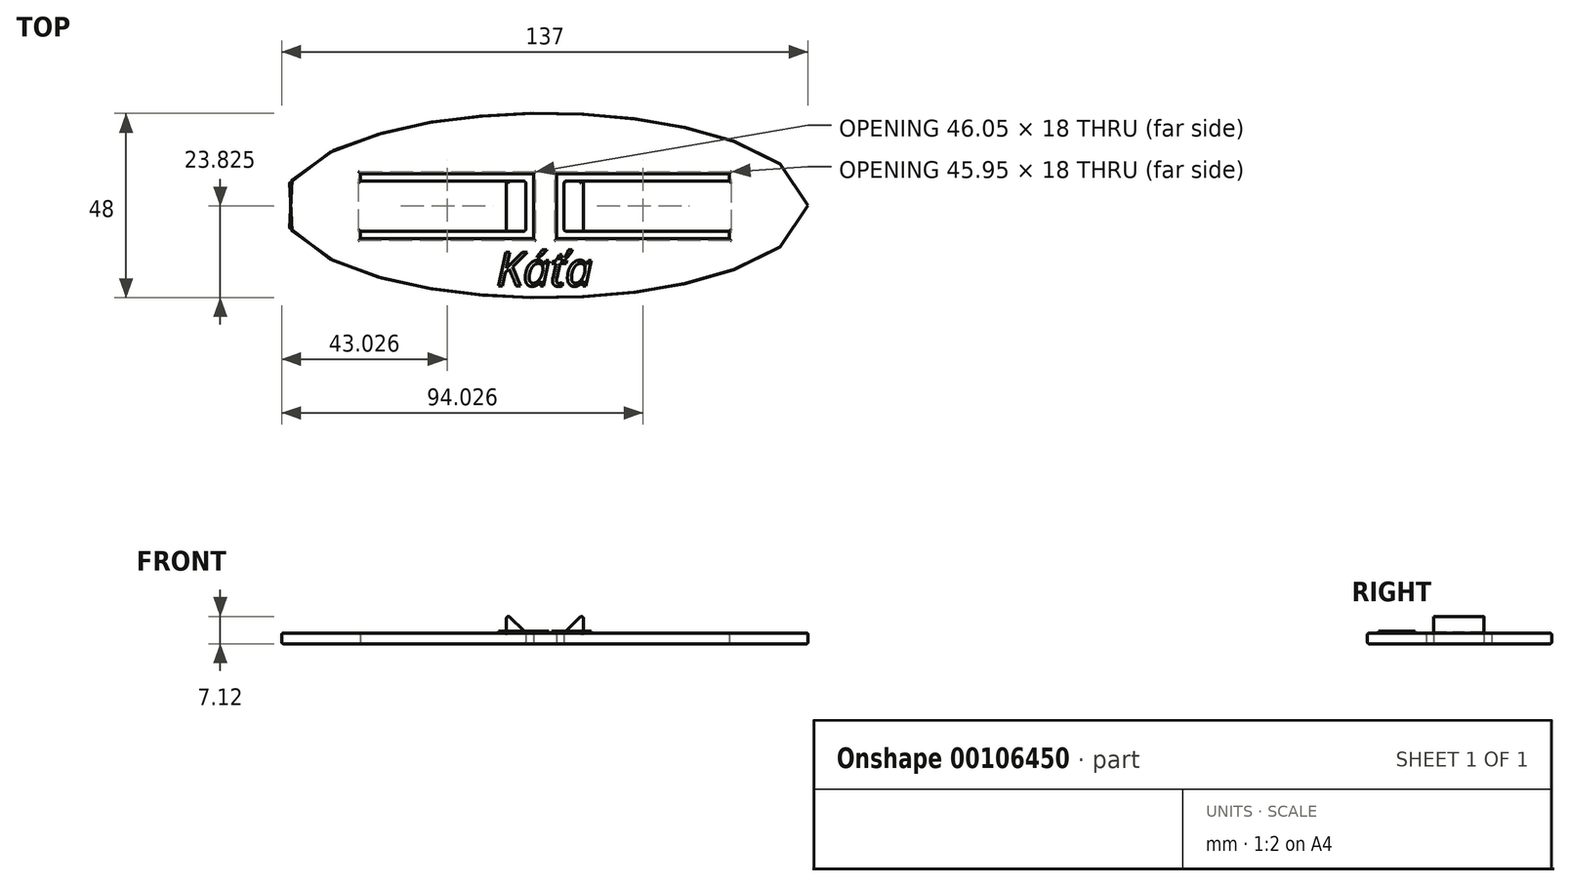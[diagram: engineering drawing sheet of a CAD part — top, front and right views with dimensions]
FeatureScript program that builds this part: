
annotation { "Feature Type Name" : "Feature", "Feature Type Description" : "" }
export const myFeature = defineFeature(function(context is Context, id is Id, definition is map)
    precondition{}
    {
        {
            var Q0;
            Q0=qCreatedBy(makeId("Top.planeOp"),FACE);
            var sketch = newSketch(context, id + "F0", { "sketchPlane" : qUnion([Q0])});
            skEllipse(sketch, "E0", {"center": v(0, 0) * mm, "majorRadius": 68.5 * mm, "minorRadius": 24 * mm, "majorAxis": v(1, 0)});
            skLineSegment(sketch, "E1", {"start": v(-5, -6.67) * mm, "end": v(-48, -6.67) * mm});
            skLineSegment(sketch, "E2", {"start": v(-48, -6.67) * mm, "end": v(-48, -8.67) * mm});
            skLineSegment(sketch, "E3", {"start": v(48, -8.67) * mm, "end": v(48, -6.67) * mm});
            skLineSegment(sketch, "E4", {"start": v(48, -6.67) * mm, "end": v(5, -6.67) * mm});
            skLineSegment(sketch, "E5", {"start": v(5, -6.67) * mm, "end": v(5, 6.33) * mm});
            skLineSegment(sketch, "E6", {"start": v(5, 6.33) * mm, "end": v(48, 6.33) * mm});
            skLineSegment(sketch, "E7", {"start": v(48, 6.33) * mm, "end": v(48, 8.33) * mm});
            skLineSegment(sketch, "E8", {"start": v(-48, 8.33) * mm, "end": v(-48, 6.33) * mm});
            skLineSegment(sketch, "E9", {"start": v(-48, 6.33) * mm, "end": v(-5, 6.33) * mm});
            skLineSegment(sketch, "E10", {"start": v(-5, 6.33) * mm, "end": v(-5, -6.67) * mm});
            skLineSegment(sketch, "E11.left", {"start": v(-2.95, 8.33) * mm, "end": v(-2.95, -8.67) * mm});
            skLineSegment(sketch, "E11.right", {"start": v(3.05, 8.33) * mm, "end": v(3.05, -8.67) * mm});
            skLineSegment(sketch, "E12", {"start": v(-48, -8.67) * mm, "end": v(-2.95, -8.67) * mm});
            skLineSegment(sketch, "E13", {"start": v(3.05, -8.67) * mm, "end": v(48, -8.67) * mm});
            skLineSegment(sketch, "E14", {"start": v(48, 8.33) * mm, "end": v(3.05, 8.33) * mm});
            skLineSegment(sketch, "E15", {"start": v(-2.95, 8.33) * mm, "end": v(-48, 8.33) * mm});
            skLineSegment(sketch, "E16", {"start": v(-70.2, 0) * mm, "end": v(71.44, 0) * mm, "construction": true});
            skPoint(sketch, "E16.endSnap0", {"position": v(68.5, 0) * mm});
            skLineSegment(sketch, "E17", {"start": v(0, -24) * mm, "end": v(71.65, -24) * mm, "construction": true});
            skLineSegment(sketch, "E18", {"start": v(-6.89, -6.67) * mm, "end": v(-6.89, 6.33) * mm, "construction": true});
            skLineSegment(sketch, "E19", {"start": v(7.19, -6.67) * mm, "end": v(7.19, 6.33) * mm, "construction": true});
            skSolve(sketch);
        }
        {
            var Q0;
            Q0=makeQuery(id+"F0.imprint","IMPRINT",FACE,{"disambiguationData":[TD([[makeQuery(id+"F0.imprint","IMPRINT",EDGE,{"derivedFrom":sQuery(id+"F0.wireOp",EDGE,"E0")}),1.0]])]});
            var Q1;
            Q1 = qSketchRegion(id + "F2", true);
            extrude(context, id + "F1", {"entities" : qUnion([Q0, Q1]), "endBound" : BoundingType.SYMMETRIC, "depth" : 2.8 * mm});
        }
        {
            var Q0;
            Q0=makeQuery(id+"F1.opExtrude","CAP_FACE",FACE,{"disambiguationData":[OSD([sQuery(id+"F0.wireOp",EDGE,"E0"),sQuery(id+"F0.wireOp",EDGE,"E1"),sQuery(id+"F0.wireOp",EDGE,"E2"),sQuery(id+"F0.wireOp",EDGE,"E3"),sQuery(id+"F0.wireOp",EDGE,"E4"),sQuery(id+"F0.wireOp",EDGE,"E5"),sQuery(id+"F0.wireOp",EDGE,"E6"),sQuery(id+"F0.wireOp",EDGE,"E7"),sQuery(id+"F0.wireOp",EDGE,"E8"),sQuery(id+"F0.wireOp",EDGE,"E9"),sQuery(id+"F0.wireOp",EDGE,"E10"),sQuery(id+"F0.wireOp",EDGE,"E11.left"),sQuery(id+"F0.wireOp",EDGE,"E11.right"),sQuery(id+"F0.wireOp",EDGE,"E12"),sQuery(id+"F0.wireOp",EDGE,"E13"),sQuery(id+"F0.wireOp",EDGE,"E14"),sQuery(id+"F0.wireOp",EDGE,"E15")])],"isStart":false});
            var sketch = newSketch(context, id + "F2", { "sketchPlane" : qUnion([Q0])});
            skLineSegment(sketch, "E20.bottom", {"start": v(-10, 6.33) * mm, "end": v(-5, 6.33) * mm});
            skLineSegment(sketch, "E20.top", {"start": v(-10, -6.67) * mm, "end": v(-5, -6.67) * mm});
            skLineSegment(sketch, "E20.left", {"start": v(-10, 6.33) * mm, "end": v(-10, -6.67) * mm});
            skLineSegment(sketch, "E20.right", {"start": v(-5, 6.33) * mm, "end": v(-5, -6.67) * mm});
            skLineSegment(sketch, "E21.bottom", {"start": v(5, 6.33) * mm, "end": v(10, 6.33) * mm});
            skLineSegment(sketch, "E21.top", {"start": v(5, -6.67) * mm, "end": v(10, -6.67) * mm});
            skLineSegment(sketch, "E21.left", {"start": v(5, 6.33) * mm, "end": v(5, -6.67) * mm});
            skLineSegment(sketch, "E21.right", {"start": v(10, 6.33) * mm, "end": v(10, -6.67) * mm});
            skSolve(sketch);
        }
        {
            var Q0;
            Q0=makeQuery(id+"F2.imprint","IMPRINT",FACE,{"disambiguationData":[TD([[makeQuery(id+"F2.imprint","IMPRINT",EDGE,{"derivedFrom":sQuery(id+"F2.wireOp",EDGE,"E20.bottom")}),-1.0]])]});
            extrude(context, id + "F3", {"entities" : qUnion([Q0]), "operationType" : NewBodyOperationType.ADD, "depth" : 5 * mm});
        }
        {
            var Q0;
            Q0=makeQuery(id+"F2.imprint","IMPRINT",FACE,{"disambiguationData":[TD([[makeQuery(id+"F2.imprint","IMPRINT",EDGE,{"derivedFrom":sQuery(id+"F2.wireOp",EDGE,"E21.bottom")}),-1.0]])]});
            extrude(context, id + "F4", {"entities" : qUnion([Q0]), "operationType" : NewBodyOperationType.ADD, "depth" : 5 * mm});
        }
        {
            var Q0;
            Q0=makeQuery(id+"F3.boolean.opBoolean","MERGE",FACE,{"derivedFrom":[makeQuery(id+"F1.opExtrude","SWEPT_FACE",FACE,{"disambiguationData":[OSD([sQuery(id+"F0.wireOp",EDGE,"E1")])]}),makeQuery(id+"F3.opExtrude","SWEPT_FACE",FACE,{"disambiguationData":[OSD([sQuery(id+"F2.wireOp",EDGE,"E20.top")])]})]});
            var sketch = newSketch(context, id + "F5", { "sketchPlane" : qUnion([Q0])});
            skLineSegment(sketch, "E22", {"start": v(-5, 1.57) * mm, "end": v(-10, 6.4) * mm});
            skSolve(sketch);
        }
        {
            var Q0;
            {var subQ0=sQuery(id+"F5.wireOp",EDGE,"E22");Q0=makeQuery(id+"F5.imprint","IMPRINT",FACE,{"disambiguationData":[TD([[makeQuery(id+"F5.imprint","IMPRINT",EDGE,{"derivedFrom":subQ0}),-1.0]])]});}
            extrude(context, id + "F6", {"entities" : qUnion([Q0]), "operationType" : NewBodyOperationType.REMOVE, "oppositeDirection" : true, "depth" : 25 * mm});
        }
        {
            var Q0;
            Q0=makeQuery(id+"F4.boolean.opBoolean","MERGE",FACE,{"derivedFrom":[makeQuery(id+"F1.opExtrude","SWEPT_FACE",FACE,{"disambiguationData":[OSD([sQuery(id+"F0.wireOp",EDGE,"E4")])]}),makeQuery(id+"F4.opExtrude","SWEPT_FACE",FACE,{"disambiguationData":[OSD([sQuery(id+"F2.wireOp",EDGE,"E21.top")])]})]});
            var sketch = newSketch(context, id + "F7", { "sketchPlane" : qUnion([Q0])});
            skLineSegment(sketch, "E23", {"start": v(10, 6.4) * mm, "end": v(5, 1.5) * mm});
            skSolve(sketch);
        }
        {
            var Q0;
            {var subQ0=sQuery(id+"F7.wireOp",EDGE,"E23");Q0=makeQuery(id+"F7.imprint","IMPRINT",FACE,{"disambiguationData":[TD([[makeQuery(id+"F7.imprint","IMPRINT",EDGE,{"derivedFrom":subQ0}),-1.0]])]});}
            extrude(context, id + "F8", {"entities" : qUnion([Q0]), "operationType" : NewBodyOperationType.REMOVE, "oppositeDirection" : true, "depth" : 25 * mm});
        }
        {
            var Q0;
            Q0=makeQuery(id+"F1.opExtrude","CAP_EDGE",EDGE,{"disambiguationData":[OSD([sQuery(id+"F0.wireOp",EDGE,"E0")])],"isStart":false});
            var Q1;
            Q1=makeQuery(id+"F1.opExtrude","CAP_EDGE",EDGE,{"disambiguationData":[OSD([sQuery(id+"F0.wireOp",EDGE,"E0")])],"isStart":true});
            var Q2;
            Q2=makeQuery(id+"F1.opExtrude","CAP_EDGE",EDGE,{"disambiguationData":[OSD([sQuery(id+"F0.wireOp",EDGE,"E13")])],"isStart":false});
            var Q3;
            Q3=makeQuery(id+"F1.opExtrude","CAP_EDGE",EDGE,{"disambiguationData":[OSD([sQuery(id+"F0.wireOp",EDGE,"E4")])],"isStart":false});
            var Q4;
            Q4=makeQuery(id+"F1.opExtrude","CAP_EDGE",EDGE,{"disambiguationData":[OSD([sQuery(id+"F0.wireOp",EDGE,"E3")])],"isStart":false});
            var Q5;
            Q5=makeQuery(id+"F8.boolean.opBoolean","COPY",EDGE,{"derivedFrom":makeQuery(id+"F8.opExtrude","CAP_EDGE",EDGE,{"disambiguationData":[OSD([sQuery(id+"F7.wireOp",EDGE,"E23")])],"isStart":true})});
            var Q6;
            Q6=makeQuery(id+"F4.boolean.opBoolean","MERGE",EDGE,{"derivedFrom":[makeQuery(id+"F1.opExtrude","SWEPT_EDGE",EDGE,{"disambiguationData":[OSD([sQuery(id+"F0.wireOp",EDGE,"E4"),sQuery(id+"F0.wireOp",EDGE,"E5")])]}),makeQuery(id+"F4.opExtrude","SWEPT_EDGE",EDGE,{"disambiguationData":[OSD([sQuery(id+"F2.wireOp",EDGE,"E21.top"),sQuery(id+"F2.wireOp",EDGE,"E21.left")])]})]});
            var Q7;
            Q7=makeQuery(id+"F8.boolean.opBoolean","COPY",EDGE,{"derivedFrom":makeQuery(id+"F8.opExtrude","SWEPT_EDGE",EDGE,{"disambiguationData":[OSD([sQuery(id+"F0.wireOp",EDGE,"E4"),sQuery(id+"F0.wireOp",EDGE,"E5"),sQuery(id+"F2.wireOp",EDGE,"E21.top"),sQuery(id+"F2.wireOp",EDGE,"E21.left"),sQuery(id+"F7.wireOp",EDGE,"E23")])]})});
            var Q8;
            Q8=makeQuery(id+"F8.boolean.opBoolean","INTERSECT",EDGE,{"derivedFrom":[makeQuery(id+"F4.boolean.opBoolean","MERGE",FACE,{"derivedFrom":[makeQuery(id+"F1.opExtrude","SWEPT_FACE",FACE,{"disambiguationData":[OSD([sQuery(id+"F0.wireOp",EDGE,"E6")])]}),makeQuery(id+"F4.opExtrude","SWEPT_FACE",FACE,{"disambiguationData":[OSD([sQuery(id+"F2.wireOp",EDGE,"E21.bottom")])]})]}),makeQuery(id+"F8.opExtrude","SWEPT_FACE",FACE,{"disambiguationData":[OSD([sQuery(id+"F7.wireOp",EDGE,"E23")])]})]});
            var Q9;
            Q9=makeQuery(id+"F6.boolean.opBoolean","COPY",EDGE,{"derivedFrom":makeQuery(id+"F6.opExtrude","SWEPT_EDGE",EDGE,{"disambiguationData":[OSD([sQuery(id+"F0.wireOp",EDGE,"E1"),sQuery(id+"F0.wireOp",EDGE,"E10"),sQuery(id+"F2.wireOp",EDGE,"E20.top"),sQuery(id+"F2.wireOp",EDGE,"E20.right"),sQuery(id+"F5.wireOp",EDGE,"E22")])]})});
            var Q10;
            Q10=makeQuery(id+"F6.boolean.opBoolean","INTERSECT",EDGE,{"derivedFrom":[makeQuery(id+"F3.boolean.opBoolean","MERGE",FACE,{"derivedFrom":[makeQuery(id+"F1.opExtrude","SWEPT_FACE",FACE,{"disambiguationData":[OSD([sQuery(id+"F0.wireOp",EDGE,"E9")])]}),makeQuery(id+"F3.opExtrude","SWEPT_FACE",FACE,{"disambiguationData":[OSD([sQuery(id+"F2.wireOp",EDGE,"E20.bottom")])]})]}),makeQuery(id+"F6.opExtrude","SWEPT_FACE",FACE,{"disambiguationData":[OSD([sQuery(id+"F5.wireOp",EDGE,"E22")])]})]});
            var Q11;
            {var subQ0=sQuery(id+"F2.wireOp",EDGE,"E20.left");Q11=makeQuery(id+"F6.boolean.opBoolean","MERGE",EDGE,{"derivedFrom":[makeQuery(id+"F3.opExtrude","CAP_EDGE",EDGE,{"disambiguationData":[OSD([subQ0])],"isStart":false}),makeQuery(id+"F6.opExtrude","SWEPT_EDGE",EDGE,{"disambiguationData":[OSD([sQuery(id+"F0.wireOp",EDGE,"E1"),sQuery(id+"F2.wireOp",EDGE,"E20.top"),subQ0,sQuery(id+"F5.wireOp",EDGE,"E22")])]})]});}
            var Q12;
            Q12=makeQuery(id+"F6.boolean.opBoolean","COPY",EDGE,{"derivedFrom":makeQuery(id+"F6.opExtrude","CAP_EDGE",EDGE,{"disambiguationData":[OSD([sQuery(id+"F5.wireOp",EDGE,"E22")])],"isStart":true})});
            var Q13;
            {var subQ0=sQuery(id+"F2.wireOp",EDGE,"E21.right");Q13=makeQuery(id+"F8.boolean.opBoolean","MERGE",EDGE,{"derivedFrom":[makeQuery(id+"F4.opExtrude","CAP_EDGE",EDGE,{"disambiguationData":[OSD([subQ0])],"isStart":false}),makeQuery(id+"F8.opExtrude","SWEPT_EDGE",EDGE,{"disambiguationData":[OSD([sQuery(id+"F0.wireOp",EDGE,"E4"),sQuery(id+"F2.wireOp",EDGE,"E21.top"),subQ0,sQuery(id+"F7.wireOp",EDGE,"E23")])]})]});}
            var Q14;
            Q14=makeQuery(id+"F1.opExtrude","CAP_EDGE",EDGE,{"disambiguationData":[OSD([sQuery(id+"F0.wireOp",EDGE,"E11.left")])],"isStart":false});
            var Q15;
            Q15=makeQuery(id+"F1.opExtrude","CAP_EDGE",EDGE,{"disambiguationData":[OSD([sQuery(id+"F0.wireOp",EDGE,"E11.right")])],"isStart":false});
            var Q16;
            Q16=makeQuery(id+"F1.opExtrude","CAP_EDGE",EDGE,{"disambiguationData":[OSD([sQuery(id+"F0.wireOp",EDGE,"E14")])],"isStart":false});
            var Q17;
            Q17=makeQuery(id+"F1.opExtrude","CAP_EDGE",EDGE,{"disambiguationData":[OSD([sQuery(id+"F0.wireOp",EDGE,"E6")])],"isStart":false});
            var Q18;
            Q18=makeQuery(id+"F1.opExtrude","CAP_EDGE",EDGE,{"disambiguationData":[OSD([sQuery(id+"F0.wireOp",EDGE,"E7")])],"isStart":false});
            var Q19;
            Q19=makeQuery(id+"F1.opExtrude","CAP_EDGE",EDGE,{"disambiguationData":[OSD([sQuery(id+"F0.wireOp",EDGE,"E15")])],"isStart":false});
            var Q20;
            Q20=makeQuery(id+"F1.opExtrude","CAP_EDGE",EDGE,{"disambiguationData":[OSD([sQuery(id+"F0.wireOp",EDGE,"E9")])],"isStart":false});
            var Q21;
            Q21=makeQuery(id+"F1.opExtrude","CAP_EDGE",EDGE,{"disambiguationData":[OSD([sQuery(id+"F0.wireOp",EDGE,"E1")])],"isStart":false});
            var Q22;
            Q22=makeQuery(id+"F1.opExtrude","CAP_EDGE",EDGE,{"disambiguationData":[OSD([sQuery(id+"F0.wireOp",EDGE,"E12")])],"isStart":false});
            var Q23;
            Q23=makeQuery(id+"F1.opExtrude","CAP_EDGE",EDGE,{"disambiguationData":[OSD([sQuery(id+"F0.wireOp",EDGE,"E2")])],"isStart":false});
            var Q24;
            Q24=makeQuery(id+"F1.opExtrude","CAP_EDGE",EDGE,{"disambiguationData":[OSD([sQuery(id+"F0.wireOp",EDGE,"E8")])],"isStart":false});
            var Q25;
            Q25=makeQuery(id+"F1.opExtrude","CAP_EDGE",EDGE,{"disambiguationData":[OSD([sQuery(id+"F0.wireOp",EDGE,"E15")])],"isStart":true});
            var Q26;
            Q26=makeQuery(id+"F1.opExtrude","CAP_EDGE",EDGE,{"disambiguationData":[OSD([sQuery(id+"F0.wireOp",EDGE,"E11.left")])],"isStart":true});
            var Q27;
            Q27=makeQuery(id+"F3.boolean.opBoolean","MERGE",EDGE,{"derivedFrom":[makeQuery(id+"F1.opExtrude","SWEPT_EDGE",EDGE,{"disambiguationData":[OSD([sQuery(id+"F0.wireOp",EDGE,"E9"),sQuery(id+"F0.wireOp",EDGE,"E10")])]}),makeQuery(id+"F3.opExtrude","SWEPT_EDGE",EDGE,{"disambiguationData":[OSD([sQuery(id+"F2.wireOp",EDGE,"E20.bottom"),sQuery(id+"F2.wireOp",EDGE,"E20.right")])]})]});
            var Q28;
            Q28=makeQuery(id+"F1.opExtrude","CAP_EDGE",EDGE,{"disambiguationData":[OSD([sQuery(id+"F0.wireOp",EDGE,"E8")])],"isStart":true});
            var Q29;
            Q29=makeQuery(id+"F1.opExtrude","CAP_EDGE",EDGE,{"disambiguationData":[OSD([sQuery(id+"F0.wireOp",EDGE,"E9")])],"isStart":true});
            var Q30;
            Q30=makeQuery(id+"F1.opExtrude","CAP_EDGE",EDGE,{"disambiguationData":[OSD([sQuery(id+"F0.wireOp",EDGE,"E2")])],"isStart":true});
            var Q31;
            Q31=makeQuery(id+"F1.opExtrude","CAP_EDGE",EDGE,{"disambiguationData":[OSD([sQuery(id+"F0.wireOp",EDGE,"E12")])],"isStart":true});
            var Q32;
            Q32=makeQuery(id+"F1.opExtrude","CAP_EDGE",EDGE,{"disambiguationData":[OSD([sQuery(id+"F0.wireOp",EDGE,"E10")])],"isStart":true});
            var Q33;
            Q33=makeQuery(id+"F1.opExtrude","CAP_FACE",FACE,{"disambiguationData":[OSD([sQuery(id+"F0.wireOp",EDGE,"E0"),sQuery(id+"F0.wireOp",EDGE,"E1"),sQuery(id+"F0.wireOp",EDGE,"E2"),sQuery(id+"F0.wireOp",EDGE,"E3"),sQuery(id+"F0.wireOp",EDGE,"E4"),sQuery(id+"F0.wireOp",EDGE,"E5"),sQuery(id+"F0.wireOp",EDGE,"E6"),sQuery(id+"F0.wireOp",EDGE,"E7"),sQuery(id+"F0.wireOp",EDGE,"E8"),sQuery(id+"F0.wireOp",EDGE,"E9"),sQuery(id+"F0.wireOp",EDGE,"E10"),sQuery(id+"F0.wireOp",EDGE,"E11.left"),sQuery(id+"F0.wireOp",EDGE,"E11.right"),sQuery(id+"F0.wireOp",EDGE,"E12"),sQuery(id+"F0.wireOp",EDGE,"E13"),sQuery(id+"F0.wireOp",EDGE,"E14"),sQuery(id+"F0.wireOp",EDGE,"E15")])],"isStart":true});
            fillet(context, id + "F9", {"entities" : qUnion([Q0, Q1, Q2, Q3, Q4, Q5, Q6, Q7, Q8, Q9, Q10, Q11, Q12, Q13, Q14, Q15, Q16, Q17, Q18, Q19, Q20, Q21, Q22, Q23, Q24, Q25, Q26, Q27, Q28, Q29, Q30, Q31, Q32, Q33]), "radius" : 0.5 * mm, "allowEdgeOverflow" : false});
        }
        {
            var Q0;
            Q0=makeQuery(id+"F3.boolean.opBoolean","MERGE",EDGE,{"derivedFrom":[makeQuery(id+"F1.opExtrude","SWEPT_EDGE",EDGE,{"disambiguationData":[OSD([sQuery(id+"F0.wireOp",EDGE,"E1"),sQuery(id+"F0.wireOp",EDGE,"E10")])]}),makeQuery(id+"F3.opExtrude","SWEPT_EDGE",EDGE,{"disambiguationData":[OSD([sQuery(id+"F2.wireOp",EDGE,"E20.top"),sQuery(id+"F2.wireOp",EDGE,"E20.right")])]})]});
            var Q1;
            Q1=makeQuery(id+"F9.opFillet","BLEND_EDGE",EDGE,{"blendedFrom":[makeQuery(id+"F1.opExtrude","CAP_EDGE",EDGE,{"disambiguationData":[OSD([sQuery(id+"F0.wireOp",EDGE,"E5")])],"isStart":true}),makeQuery(id+"F1.opExtrude","CAP_EDGE",EDGE,{"disambiguationData":[OSD([sQuery(id+"F0.wireOp",EDGE,"E6")])],"isStart":true})],"blendedInto":[]});
            fillet(context, id + "F10", {"entities" : qUnion([Q0, Q1]), "radius" : 0.5 * mm, "tangentPropagation" : true, "allowEdgeOverflow" : false});
        }
        {
            var Q0;
            {var subQ4=sQuery(id+"F2.wireOp",EDGE,"E20.left");Q0=makeQuery(id+"F2.imprint","IMPRINT",FACE,{"disambiguationData":[TD([[makeQuery(id+"F2.imprint","IMPRINT",EDGE,{"derivedFrom":subQ4}),-1.0]])]});}
            var sketch = newSketch(context, id + "F11", { "sketchPlane" : qUnion([Q0])});
            skText(sketch, "E24", { "text": "Káťa\n", "fontName": "OpenSans-Italic.ttf"});
            const initialGuessF11  = {"E24": [-0.01259, -0.02097, 1, 0, 0.0089]};
            skSetInitialGuess(sketch, initialGuessF11);
            skSolve(sketch);
        }
        {
            var Q0;
            Q0 = qSketchRegion(id + "F11", true);
            extrude(context, id + "F12", {"entities" : qUnion([Q0]), "operationType" : NewBodyOperationType.ADD, "depth" : 0.5 * mm});
        }
    });
